# Revit family: HB-8000C-A
name_source: partatom
category: 衛工裝置
revit_build: Autodesk Revit 2015 (Build: 20140223_1515(x64)
units: mm (PartAtom-declared; Revit-internal decimal feet)

## types (1)
- HB-8000C-A
    ADA Compliance = Yes - Flush Valve
    Back Up Power = None
    Brushed Nickel (PVD) Valve Finish = 否
    CL of Supply Above Top of Fixture = 11 1/2"
    CL of Supply to Centerline of Valve = 4 3/4"
    CW 接頭 = 是
    Flush Choice = Single Flush
    Flush Cycle Water Usage = 1.6 gpf / 6.0 Lpf
    HW 接頭 = 否
    Inlet Spud Size = 1-1/2" I.P.S.
    Inlet Supply Size = 1"
    Manual Override = 是
    Mounting = Exposed
    OA Height Above Top of Fixture = 16"
    Operation = Automatic
    Polished Brass (PVD) Valve Finish = 是
    Polished Chrome Valve Finish = 是
    Power Source = AA Alkaline Battery x 4 pcs
    Sensor Type = Active Infrared
    Spud Location = Exposed Top
    URL = www.hydrotekintl.com
    Valve Body = Chrome Plated
    Valve Body, Tailpiece and Control Stop = Semi-Red Brass, ASSE 1037, ANSI/ASME A112.19.2
    Valve Cover = Engineered Metal
    Valve Type = Piston
    Warranty = 3 Years (Limited)
    廢水口接頭 = 否
    描述 = Exposed, Hard Wired, Sensor Operated H-8000C-A Water Closet Flush Valve
    模型 = HB-8000C-A
    製造商 = Hydrotek International, Inc.
    通風口接頭 = 否
    關鍵註記 = Sensor Operated Flush Valve for Toilet

## geometry (parser evidence)
native form markers: Sweep x8
no freeform markers — native parametric forms only
